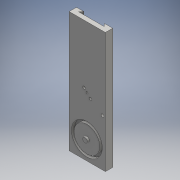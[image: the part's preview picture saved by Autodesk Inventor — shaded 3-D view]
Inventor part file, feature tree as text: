
AUTODESK INVENTOR PART (.ipt)
format: ipt  version: 2016 (Build 200138000, 138)  size: 195,072 bytes
history: native  units: mm
features: extrude x7, sketch x6, hole x3, thread x1
ambient origin geometry x8: Origin, YZ Plane, XZ Plane, XY Plane, X Axis, Y Axis, Z Axis, Center Point
bodies: Solid1 (feature_tree)
feature tree (17):
  extrude  "Extrusion1"  Depth=29.6mm
  sketch  "Sketch2"  dims[d2=29.9mm d4=22.68928mm]
  sketch  "Sketch3"  dims[d5=33.0mm d6=8.726646mm]
  extrude  "Extrusion2"  Depth=22.68928mm
  extrude  "Extrusion3"  Depth=8.726646mm
  extrude  "Extrusion4"  Depth=486.0mm
  sketch  "Sketch4"  dims[d7=486.0mm d8=0.0mm d9=22.0mm]
  extrude  "Extrusion5"  Depth=14.5mm
  extrude  "Extrusion7"  Depth=10.0mm
  extrude  "Extrusion8"  Depth=10.0mm
  sketch  "Sketch5"  dims[d10=124.2mm d11=14.5mm]
  sketch  "Sketch6"  dims[d12=62.1mm d13=104.0mm d14=19.02mm d15=8.2mm d17=13.0mm d18=0.0mm d19=7.5mm d20=0.0mm d21=7.5mm d22=0.0mm d23=19.0mm d24=3.7mm d25=0.0mm d26=9.4mm d29=0.0mm d30=18.7mm d31=18.7mm d36=6.0mm d37=0.0mm d38=17.0mm d39=46.5mm d40=3.0mm d41=0.0mm d42=10.0mm d43=225.0mm d44=60.0mm d45=11.0mm d46=60.5mm d47=250.5mm d48=11.0mm d49=190.5mm d50=11.5mm d51=8.5mm d52=6.0mm d53=11.0mm d54=8.5mm d55=90.0deg d56=8.0mm d57=20.594885mm d58=7.0mm d59=6.0mm d60=10.0mm d61=7.5mm d62=90.0deg d63=8.0mm d64=20.594885mm d65=7.5mm d66=6.0mm d67=11.0mm d68=7.0mm d69=90.0deg d70=8.0mm d71=20.594885mm d75=10.0mm d76=0.0mm]
  hole  "Hole1"  [1 undecoded]
  hole  "Hole2"  [1 undecoded]
  hole  "Hole3"  [1 undecoded]
  thread  "Thread1"  [1 undecoded]
  sketch  "Sketch1"  dims[d0=146.0mm d1=29.6mm]
note: 4 required parameter values undecoded (feature->parameter linkage not recoverable at this tier; creation-order binding heuristic only, values carry confidence <= 0.55)
